# Revit family: Site - Wood Fence - P - LB
name_source: partatom
category: Site
revit_build: Autodesk Revit 2013 (Build: 20130531_2115(x64)
units: mm (PartAtom-declared; Revit-internal decimal feet)

## types (1)
- Site - Wood Fence - P - LB
    Cap = <By Category>
    Center Rail = No
    Max Post Spacing = 1500 mm  [stored 4.92126 ft]
    Plank = <By Category>
    Plank Gap = 12 mm  [stored 0.0393701 ft]
    Plank Height = 1525 mm  [stored 5.00328 ft]
    Plank Height Above Ground = 50 mm  [stored 0.164042 ft]
    Plank Thickness = 16 mm  [stored 0.0524934 ft]
    Plank Width = 152 mm  [stored 0.498688 ft]
    Post = <By Category>
    Post Size = 102 mm
    Rail = <By Category>
    Rail Height = 85 mm
    Rail Top Bottom Offset = 200 mm  [stored 0.656168 ft]
    Rail Width = 20 mm  [stored 0.0656168 ft]

note: [stored X ft] marks values corroborated as IEEE doubles in the binary element streams (Revit-internal decimal feet)

## geometry (parser evidence)
native form markers: Sweep x11
no freeform markers — native parametric forms only
